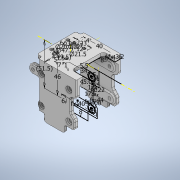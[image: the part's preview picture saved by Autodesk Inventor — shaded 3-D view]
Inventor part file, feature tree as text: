
AUTODESK INVENTOR PART (.ipt)
format: ipt  version: 2020.2 (Build 242310000, 310)  size: 825,344 bytes
history: native  units: mm
features: extrude x5, sketch x3, chamfer x3, fillet x1, mirror x1
ambient origin geometry x8: Origin, YZ Plane, XZ Plane, XY Plane, X Axis, Y Axis, Z Axis, Center Point
bodies: Solid1 (feature_tree)
feature tree (13):
  sketch  "Sketch1"  dims[d0=3.6mm d2=12.0mm]
  sketch  "Sketch3"  dims[d8=21.5mm d9=40.0mm d10=47.2mm d11=4.0mm d12=4.0mm d13=0.0mm d16=5.5mm d17=34.0mm d18=34.0mm d19=46.0mm d20=51.5mm d21=44.0mm d22=22.0mm d23=3.5mm d26=23.0mm d29=4.0mm d32=3.2mm d33=6.0mm d37=8.0mm d39=4.0mm d40=0.0mm d42=4.0mm d44=20.0mm d49=1.0mm d50=4.0mm d51=40.0mm d52=1.5mm d54=12.0mm d55=40.0mm d56=40.0mm d57=35.0mm d58=7.5mm d61=2.8mm d62=0.0mm d63=7.0mm d67=8.0mm d68=2.4mm d69=0.0mm d71=6.0mm d72=6.0mm d77=20.0mm d78=3.6mm d79=7.0mm d83=17.5mm d84=45.0deg d85=2.0mm d87=45.0deg d88=4.5mm d89=2.0mm d90=45.0deg d91=2.0mm d98=7.0mm d99=3.6mm d100=5.0mm d101=5.0mm d102=5.0mm d103=1.0mm d105=5.5mm d106=0.0mm d107=1.0mm d108=2.0mm d109=45.0deg d110=9.5mm d111=11.0mm d112=0.2mm d113=1.5mm d114=2.0mm d115=45.0deg d30=0.5mm d31=0.872665mm d116=0.5mm d117=0.872665mm d118=0.5mm d119=0.872665mm]
  sketch  "Sketch2"  dims[d3=17.0mm d7=0.02mm]
  extrude  "Extrusion1"  Depth=12.0mm
  extrude  "Extrusion5"  Depth=0.02mm
  extrude  "Extrusion7"  Depth=11.0mm
  chamfer  "Chamfer4"  Distance=47.2mm
  extrude  "Extrusion8"  Depth=11.0mm
  extrude  "Extrusion6"  Depth=11.0mm TaperAngle=0.0deg
  fillet  "Fillet3"  Radius=5.5mm
  chamfer  "Chamfer7"  Distance=34.0mm
  chamfer  "Chamfer6"  Distance=34.0mm
  mirror  "Mirror1"
